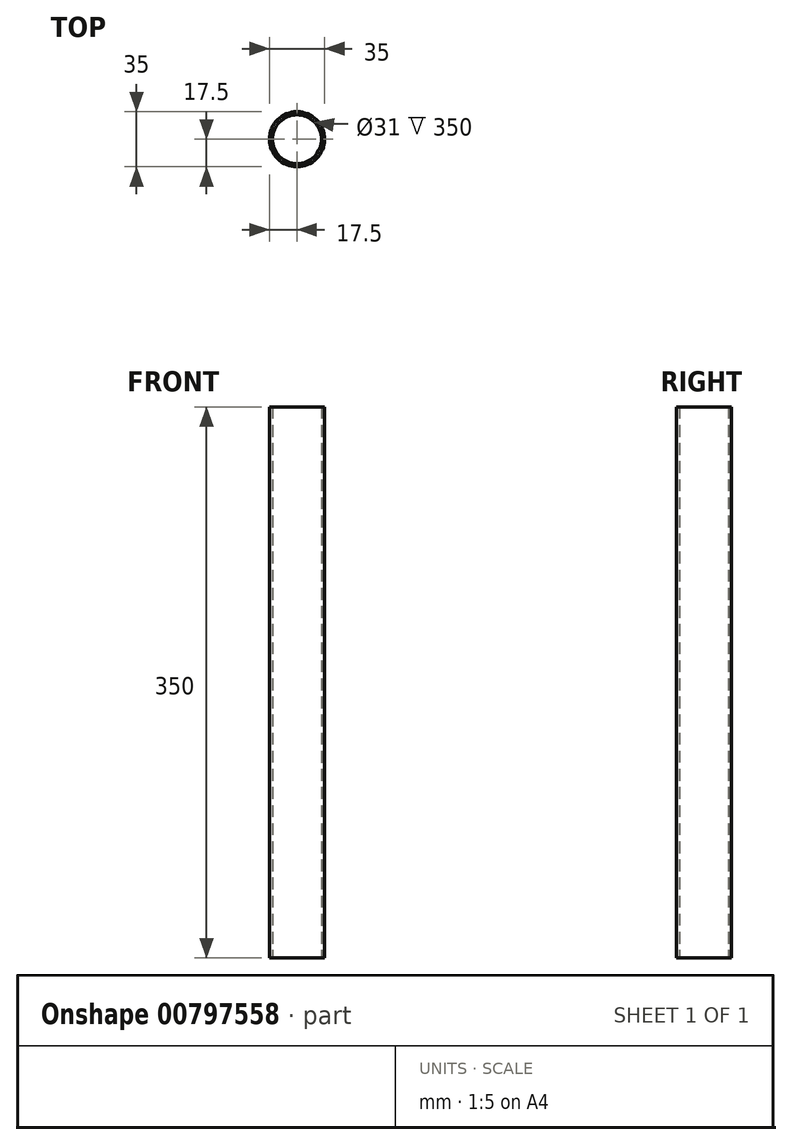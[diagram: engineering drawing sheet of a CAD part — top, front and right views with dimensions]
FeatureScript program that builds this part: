
annotation { "Feature Type Name" : "Feature", "Feature Type Description" : "" }
export const myFeature = defineFeature(function(context is Context, id is Id, definition is map)
    precondition{}
    {
        {
            var Q0;
            Q0=qCreatedBy(makeId("Top.planeOp"),FACE);
            var sketch = newSketch(context, id + "F0", { "sketchPlane" : qUnion([Q0])});
            skCircle(sketch, "E0", {"center": v(0, 0) * mm, "radius": 17.5 * mm});
            skCircle(sketch, "E1", {"center": v(0, 0) * mm, "radius": 15.5 * mm});
            skSolve(sketch);
        }
        {
            var Q0;
            Q0 = qSketchRegion(id + "F0", true);
            extrude(context, id + "F1", {"entities" : qUnion([Q0]), "depth" : 350 * mm, "offsetDistance" : 25 * mm});
        }
    });
